FCSTD DOCUMENT  (FreeCAD 0.17R12435 (Git))
Label: X2SON-4_1x1mm_P0.65mm
License: All rights reserved
LicenseURL: http://en.wikipedia.org/wiki/All_rights_reserved
objects: Sketcher::SketchObject×6, App::Annotation×2, App::DocumentObjectGroup×1
note: 6 computed .brp shape members not serialized (recipe doc carries the construction recipe); baked Part::Feature solids carry a one-line shape summary decoded from their .brp

FEATURE [App::Annotation] Text  label="Ref#_0.6mm"
  LabelText = REF**
  Position = (0,1,0)
FEATURE [App::Annotation] Text001  label="Value#_1.00mm"
  LabelText = X2SON-4_1x1mm_P0.65mm
  Position = (0,-1.5,0)
FEATURE [Sketcher::SketchObject] Sketch001  label="F_Fab_0.1"
  MapMode = 2
  sketch-geometry (9):
    g0: LineSegment [constr] StartX=-0.5 StartY=0.5 StartZ=0 EndX=0.5 EndY=0.5 EndZ=0
    g1: LineSegment [constr] StartX=0.5 StartY=0.5 StartZ=0 EndX=0.5 EndY=-0.5 EndZ=0
    g2: LineSegment [constr] StartX=0.5 StartY=-0.5 StartZ=0 EndX=-0.5 EndY=-0.5 EndZ=0
    g3: LineSegment [constr] StartX=-0.5 StartY=-0.5 StartZ=0 EndX=-0.5 EndY=0.5 EndZ=0
    g4: LineSegment StartX=0.5 StartY=-0.5 StartZ=0 EndX=-0.5 EndY=-0.5 EndZ=0
    g5: LineSegment StartX=-0.5 StartY=-0.5 StartZ=0 EndX=-0.5 EndY=0.25 EndZ=0
    g6: LineSegment StartX=-0.5 StartY=0.25 StartZ=0 EndX=-0.25 EndY=0.5 EndZ=0
    g7: LineSegment StartX=-0.25 StartY=0.5 StartZ=0 EndX=0.5 EndY=0.5 EndZ=0
    g8: LineSegment StartX=0.5 StartY=0.5 StartZ=0 EndX=0.5 EndY=-0.5 EndZ=0
  constraints (22):
    c: Coincident(g0,g1)
    c: Coincident(g1,g2)
    c: Coincident(g2,g3)
    c: Coincident(g3,g0)
    c: Horizontal(g2)
    c: Vertical(g1)
    c: Equal(g0,g3)
    c: Symmetric(g0,g2,g-1)
    c: Symmetric(g0,g0,g-2)
    c: DistanceY(g3,g3) = 1
    c: Coincident(g1,g4)
    c: Coincident(g4,g2)
    c: Coincident(g4,g5)
    c: PointOnObject(g5,g3)
    c: Coincident(g5,g6)
    c: PointOnObject(g6,g0)
    c: Coincident(g6,g7)
    c: Coincident(g7,g0)
    c: Coincident(g7,g8)
    c: Coincident(g8,g4)
    c: DistanceX(g6,g6) = 0.25
    c: DistanceY(g6,g6) = 0.25
FEATURE [Sketcher::SketchObject] Sketch004  label="Pads_Poly_mask"
  MapMode = 5
  sketch-geometry (39):
    g0: LineSegment StartX=0.339411 StartY=0 StartZ=0 EndX=0 EndY=0.339411 EndZ=0
    g1: LineSegment StartX=0 StartY=0.339411 StartZ=0 EndX=-0.339411 EndY=0 EndZ=0
    g2: LineSegment StartX=-0.339411 StartY=0 StartZ=0 EndX=0 EndY=-0.339411 EndZ=0
    g3: LineSegment StartX=0 StartY=-0.339411 StartZ=0 EndX=0.339411 EndY=0 EndZ=0
    g4: Circle [constr] CenterX=0 CenterY=0 CenterZ=0 NormalX=0 NormalY=0 NormalZ=1 AngleXU=0 Radius=0.339411
    g5: Circle CenterX=0 CenterY=0 CenterZ=0 NormalX=0 NormalY=0 NormalZ=1 AngleXU=0 Radius=0.24
    g6: LineSegment StartX=-0.61 StartY=0.43 StartZ=0 EndX=-0.25 EndY=0.43 EndZ=0
    g7: LineSegment StartX=-0.25 StartY=0.43 StartZ=0 EndX=-0.25 EndY=0.4 EndZ=0
    g8: LineSegment StartX=-0.43 StartY=0.22 StartZ=0 EndX=-0.61 EndY=0.22 EndZ=0
    g9: LineSegment StartX=-0.61 StartY=0.22 StartZ=0 EndX=-0.61 EndY=0.43 EndZ=0
    g10: LineSegment StartX=-0.43 StartY=0.22 StartZ=0 EndX=-0.25 EndY=0.4 EndZ=0
    g11: LineSegment [constr] StartX=-0.43 StartY=0.325 StartZ=0 EndX=0.43 EndY=0.325 EndZ=0
    g12: LineSegment [constr] StartX=0.43 StartY=0.325 StartZ=0 EndX=0.43 EndY=-0.325 EndZ=0
    g13: LineSegment [constr] StartX=0.43 StartY=-0.325 StartZ=0 EndX=-0.43 EndY=-0.325 EndZ=0
    g14: LineSegment [constr] StartX=-0.43 StartY=-0.325 StartZ=0 EndX=-0.43 EndY=0.325 EndZ=0
    g15: LineSegment [constr] StartX=-0.5 StartY=0.5 StartZ=0 EndX=0.5 EndY=0.5 EndZ=0
    g16: LineSegment [constr] StartX=0.5 StartY=0.5 StartZ=0 EndX=0.5 EndY=-0.5 EndZ=0
    g17: LineSegment [constr] StartX=0.5 StartY=-0.5 StartZ=0 EndX=-0.5 EndY=-0.5 EndZ=0
    g18: LineSegment [constr] StartX=-0.5 StartY=-0.5 StartZ=0 EndX=-0.5 EndY=0.5 EndZ=0
    g19: LineSegment [constr] StartX=-0.25 StartY=0.4 StartZ=0 EndX=-0.0947056 EndY=0.244706 EndZ=0
    g20: LineSegment StartX=0.61 StartY=0.43 StartZ=0 EndX=0.25 EndY=0.43 EndZ=0
    g21: LineSegment StartX=0.25 StartY=0.43 StartZ=0 EndX=0.25 EndY=0.4 EndZ=0
    g22: LineSegment StartX=0.43 StartY=0.22 StartZ=0 EndX=0.61 EndY=0.22 EndZ=0
    g23: LineSegment StartX=0.61 StartY=0.22 StartZ=0 EndX=0.61 EndY=0.43 EndZ=0
    g24: LineSegment StartX=0.43 StartY=0.22 StartZ=0 EndX=0.25 EndY=0.4 EndZ=0
    g25: LineSegment StartX=0.61 StartY=-0.43 StartZ=0 EndX=0.25 EndY=-0.43 EndZ=0
    g26: LineSegment StartX=0.25 StartY=-0.43 StartZ=0 EndX=0.25 EndY=-0.4 EndZ=0
    g27: LineSegment StartX=0.43 StartY=-0.22 StartZ=0 EndX=0.61 EndY=-0.22 EndZ=0
    g28: LineSegment StartX=0.61 StartY=-0.22 StartZ=0 EndX=0.61 EndY=-0.43 EndZ=0
    g29: LineSegment StartX=0.43 StartY=-0.22 StartZ=0 EndX=0.25 EndY=-0.4 EndZ=0
    g30: LineSegment StartX=-0.61 StartY=-0.43 StartZ=0 EndX=-0.25 EndY=-0.43 EndZ=0
    g31: LineSegment StartX=-0.25 StartY=-0.43 StartZ=0 EndX=-0.25 EndY=-0.4 EndZ=0
    g32: LineSegment StartX=-0.43 StartY=-0.22 StartZ=0 EndX=-0.61 EndY=-0.22 EndZ=0
    g33: LineSegment StartX=-0.61 StartY=-0.22 StartZ=0 EndX=-0.61 EndY=-0.43 EndZ=0
    g34: LineSegment StartX=-0.43 StartY=-0.22 StartZ=0 EndX=-0.25 EndY=-0.4 EndZ=0
    g35: Circle CenterX=0.43 CenterY=-0.325 CenterZ=0 NormalX=0 NormalY=0 NormalZ=1 AngleXU=0 Radius=0.0742462
    g36: Circle CenterX=-0.43 CenterY=-0.325 CenterZ=0 NormalX=0 NormalY=0 NormalZ=1 AngleXU=0 Radius=0.0742462
    g37: Circle CenterX=-0.43 CenterY=0.325 CenterZ=0 NormalX=0 NormalY=0 NormalZ=1 AngleXU=0 Radius=0.0742462
    g38: Circle CenterX=0.43 CenterY=0.325 CenterZ=0 NormalX=0 NormalY=0 NormalZ=1 AngleXU=0 Radius=0.0742462
  constraints (114):
    c: Coincident(g0,g1)
    c: Coincident(g1,g2)
    c: Coincident(g2,g3)
    c: Coincident(g3,g0)
    c: Equal(g0,g1)
    c: Equal(g0,g2)
    c: Equal(g0,g3)
    c: PointOnObject(g0,g4)
    c: PointOnObject(g1,g4)
    c: PointOnObject(g2,g4)
    c: PointOnObject(g3,g4)
    c: Distance(g2) = 0.48
    c: Coincident(g4,g-1)
    c: PointOnObject(g0,g-1)
    c: Coincident(g5,g-1)
    c: Coincident(g6,g7)
    c: Coincident(g8,g9)
    c: Coincident(g9,g6)
    c: Horizontal(g6)
    c: Horizontal(g8)
    c: Vertical(g7)
    c: Vertical(g9)
    c: Coincident(g10,g7)
    c: Coincident(g10,g8)
    c: Parallel(g10,g1)
    c: DistanceX(g6,g6) = 0.36
    c: DistanceY(g9,g9) = 0.21
    c: DistanceX(g8,g8) = 0.18
    c: DistanceY(g7,g7) = 0.03
    c: Coincident(g11,g12)
    c: Coincident(g12,g13)
    c: Coincident(g13,g14)
    c: Coincident(g14,g11)
    c: Vertical(g12)
    c: Vertical(g14)
    c: Symmetric(g11,g11,g-2)
    c: Symmetric(g11,g12,g-1)
    c: DistanceX(g11,g11) = 0.86
    c: Coincident(g15,g16)
    c: Coincident(g16,g17)
    c: Coincident(g17,g18)
    c: Coincident(g18,g15)
    c: Horizontal(g15)
    c: Horizontal(g17)
    c: Vertical(g16)
    c: Vertical(g18)
    c: Symmetric(g15,g15,g-2)
    c: Symmetric(g15,g17,g-1)
    c: Equal(g18,g15)
    c: DistanceY(g18,g18) = 1
    c: PointOnObject(g8,g14)
    c: Symmetric(g6,g8,g11)
    c: Coincident(g19,g7)
    c: PointOnObject(g19,g1)
    c: Perpendicular(g10,g19)
    c: Distance(g19) = 0.219619
    c: Coincident(g20,g21)
    c: Coincident(g22,g23)
    c: Coincident(g23,g20)
    c: Horizontal(g20)
    c: Horizontal(g22)
    c: Vertical(g21)
    c: Vertical(g23)
    c: Coincident(g24,g21)
    c: Coincident(g24,g22)
    c: PointOnObject(g22,g12)
    c: Symmetric(g20,g22,g11)
    c: Equal(g20,g6)
    c: Equal(g23,g9)
    c: Equal(g22,g8)
    c: Parallel(g24,g0)
    c: Coincident(g30,g31)
    c: Coincident(g32,g33)
    c: Coincident(g33,g30)
    c: Horizontal(g30)
    c: Horizontal(g32)
    c: Vertical(g31)
    c: Vertical(g33)
    c: Coincident(g34,g31)
    c: Coincident(g34,g32)
    c: Coincident(g25,g26)
    c: Coincident(g27,g28)
    c: Coincident(g28,g25)
    c: Horizontal(g25)
    c: Horizontal(g27)
    c: Vertical(g26)
    c: Vertical(g28)
    c: Coincident(g29,g26)
    c: Coincident(g29,g27)
    c: Equal(g25,g30)
    c: Equal(g28,g33)
    c: Equal(g27,g32)
    c: PointOnObject(g27,g12)
    c: Equal(g8,g27)
    c: Equal(g27,g32)
    c: Equal(g28,g33)
    c: Equal(g33,g9)
    c: Equal(g6,g30)
    c: Equal(g30,g25)
    c: PointOnObject(g32,g14)
    c: Symmetric(g32,g30,g13)
    c: Symmetric(g27,g25,g13)
    c: Parallel(g3,g29)
    c: Parallel(g2,g34)
    c: Coincident(g35,g12)
    c: Coincident(g36,g13)
    c: Coincident(g37,g11)
    c: Coincident(g38,g11)
    c: Equal(g38,g35)
    c: Equal(g35,g36)
    c: Equal(g36,g37)
    c: DistanceY(g12,g12) = 0.65
    c: Tangent(g37,g10)
    c: Tangent(g5,g3)
FEATURE [Sketcher::SketchObject] Sketch005  label="Pads_Poly"
  ExternalGeometry = -> [Sketch004]
  MapMode = 5
  sketch-geometry (38):
    g0: LineSegment StartX=0 StartY=0.410122 StartZ=0 EndX=-0.410122 EndY=0 EndZ=0
    g1: LineSegment StartX=-0.410122 StartY=0 StartZ=0 EndX=0 EndY=-0.410122 EndZ=0
    g2: LineSegment StartX=0 StartY=-0.410122 StartZ=0 EndX=0.410122 EndY=0 EndZ=0
    g3: LineSegment StartX=0.410122 StartY=0 StartZ=0 EndX=0 EndY=0.410122 EndZ=0
    g4: LineSegment [constr] StartX=-0.339411 StartY=0 StartZ=0 EndX=-0.374767 EndY=-0.0353553 EndZ=0
    g5: LineSegment StartX=-0.2 StartY=0.379289 StartZ=0 EndX=-0.2 EndY=0.48 EndZ=0
    g6: LineSegment StartX=-0.2 StartY=0.48 StartZ=0 EndX=-0.66 EndY=0.48 EndZ=0
    g7: LineSegment StartX=-0.66 StartY=0.48 StartZ=0 EndX=-0.66 EndY=0.17 EndZ=0
    g8: LineSegment StartX=-0.66 StartY=0.17 StartZ=0 EndX=-0.409289 EndY=0.17 EndZ=0
    g9: LineSegment StartX=-0.409289 StartY=0.17 StartZ=0 EndX=-0.2 EndY=0.379289 EndZ=0
    g10: LineSegment [constr] StartX=-0.25 StartY=0.4 StartZ=0 EndX=-0.214645 EndY=0.364645 EndZ=0
    g11: LineSegment StartX=0.2 StartY=0.379289 StartZ=0 EndX=0.2 EndY=0.48 EndZ=0
    g12: LineSegment StartX=0.409289 StartY=0.17 StartZ=0 EndX=0.2 EndY=0.379289 EndZ=0
    g13: LineSegment StartX=0.66 StartY=0.17 StartZ=0 EndX=0.409289 EndY=0.17 EndZ=0
    g14: LineSegment StartX=0.66 StartY=0.48 StartZ=0 EndX=0.66 EndY=0.17 EndZ=0
    g15: LineSegment StartX=0.2 StartY=0.48 StartZ=0 EndX=0.66 EndY=0.48 EndZ=0
    g16: LineSegment StartX=0.2 StartY=-0.48 StartZ=0 EndX=0.66 EndY=-0.48 EndZ=0
    g17: LineSegment StartX=0.2 StartY=-0.379289 StartZ=0 EndX=0.2 EndY=-0.48 EndZ=0
    g18: LineSegment StartX=0.409289 StartY=-0.17 StartZ=0 EndX=0.2 EndY=-0.379289 EndZ=0
    g19: LineSegment StartX=0.66 StartY=-0.17 StartZ=0 EndX=0.409289 EndY=-0.17 EndZ=0
    g20: LineSegment StartX=0.66 StartY=-0.48 StartZ=0 EndX=0.66 EndY=-0.17 EndZ=0
    g21: LineSegment StartX=-0.409289 StartY=-0.17 StartZ=0 EndX=-0.2 EndY=-0.379289 EndZ=0
    g22: LineSegment StartX=-0.2 StartY=-0.379289 StartZ=0 EndX=-0.2 EndY=-0.48 EndZ=0
    g23: LineSegment StartX=-0.2 StartY=-0.48 StartZ=0 EndX=-0.66 EndY=-0.48 EndZ=0
    g24: LineSegment StartX=-0.66 StartY=-0.48 StartZ=0 EndX=-0.66 EndY=-0.17 EndZ=0
    g25: LineSegment StartX=-0.66 StartY=-0.17 StartZ=0 EndX=-0.409289 EndY=-0.17 EndZ=0
    g26: LineSegment [constr] StartX=0.25 StartY=0.4 StartZ=0 EndX=0.214645 EndY=0.364645 EndZ=0
    g27: LineSegment [constr] StartX=0.25 StartY=-0.4 StartZ=0 EndX=0.214645 EndY=-0.364645 EndZ=0
    g28: LineSegment [constr] StartX=-0.25 StartY=-0.4 StartZ=0 EndX=-0.214645 EndY=-0.364645 EndZ=0
    g29: LineSegment [constr] StartX=-0.61 StartY=0.43 StartZ=0 EndX=-0.61 EndY=0.48 EndZ=0
    g30: LineSegment [constr] StartX=0.61 StartY=0.43 StartZ=0 EndX=0.61 EndY=0.48 EndZ=0
    g31: LineSegment [constr] StartX=0.61 StartY=-0.43 StartZ=0 EndX=0.61 EndY=-0.48 EndZ=0
    g32: LineSegment [constr] StartX=-0.61 StartY=-0.43 StartZ=0 EndX=-0.61 EndY=-0.48 EndZ=0
    g33: Circle CenterX=-0.43 CenterY=0.325 CenterZ=0 NormalX=0 NormalY=0 NormalZ=1 AngleXU=0 Radius=0.124246
    g34: Circle CenterX=0.43 CenterY=0.325 CenterZ=0 NormalX=0 NormalY=0 NormalZ=1 AngleXU=0 Radius=0.124246
    g35: Circle CenterX=0.43 CenterY=-0.325 CenterZ=0 NormalX=0 NormalY=0 NormalZ=1 AngleXU=0 Radius=0.124246
    g36: Circle CenterX=-0.43 CenterY=-0.325 CenterZ=0 NormalX=0 NormalY=0 NormalZ=1 AngleXU=0 Radius=0.124246
    g37: Circle CenterX=0 CenterY=0 CenterZ=0 NormalX=0 NormalY=0 NormalZ=1 AngleXU=0 Radius=0.29
  constraints (109):
    c: PointOnObject(g0,g-2)
    c: PointOnObject(g0,g-1)
    c: Coincident(g0,g1)
    c: PointOnObject(g1,g-2)
    c: Coincident(g1,g2)
    c: Coincident(g2,g3)
    c: Coincident(g3,g0)
    c: PointOnObject(g2,g-1)
    c: Parallel(g2,g-19)
    c: Parallel(g-19,g0)
    c: Parallel(g-21,g1)
    c: PointOnObject(g4,g1)
    c: Perpendicular(g-21,g4)
    c: Distance(g4) = 0.05
    c: Coincident(g4,g-21)
    c: Vertical(g5)
    c: Coincident(g5,g6)
    c: Horizontal(g6)
    c: Coincident(g6,g7)
    c: Vertical(g7)
    c: Coincident(g7,g8)
    c: Horizontal(g8)
    c: Coincident(g8,g9)
    c: Coincident(g9,g5)
    c: Parallel(g9,g-7)
    c: DistanceY(g-9,g6) = 0.05
    c: DistanceX(g6,g-9) = 0.05
    c: DistanceY(g7,g-9) = 0.05
    c: DistanceX(g-8,g5) = 0.05
    c: Coincident(g10,g-7)
    c: PointOnObject(g10,g9)
    c: Perpendicular(g-7,g10)
    c: Distance(g10) = 0.05
    c: Vertical(g11)
    c: Coincident(g11,g15)
    c: Horizontal(g15)
    c: Coincident(g15,g14)
    c: Vertical(g14)
    c: Coincident(g14,g13)
    c: Horizontal(g13)
    c: Coincident(g13,g12)
    c: Coincident(g12,g11)
    c: Vertical(g22)
    c: Coincident(g22,g23)
    c: Horizontal(g23)
    c: Coincident(g23,g24)
    c: Vertical(g24)
    c: Coincident(g24,g25)
    c: Horizontal(g25)
    c: Coincident(g25,g21)
    c: Coincident(g21,g22)
    c: Vertical(g17)
    c: Coincident(g17,g16)
    c: Horizontal(g16)
    c: Coincident(g16,g20)
    c: Vertical(g20)
    c: Coincident(g20,g19)
    c: Horizontal(g19)
    c: Coincident(g19,g18)
    c: Coincident(g18,g17)
    c: Equal(g24,g7)
    c: Equal(g7,g14)
    c: Equal(g14,g20)
    c: Equal(g16,g23)
    c: Equal(g23,g6)
    c: Equal(g6,g15)
    c: Equal(g8,g25)
    c: Equal(g25,g19)
    c: Equal(g19,g13)
    c: Equal(g11,g5)
    c: Equal(g5,g22)
    c: Equal(g22,g17)
    c: Coincident(g26,g-12)
    c: PointOnObject(g26,g12)
    c: Coincident(g27,g-18)
    c: PointOnObject(g27,g18)
    c: Coincident(g28,g-17)
    c: PointOnObject(g28,g21)
    c: Perpendicular(g-17,g28)
    c: Perpendicular(g-18,g27)
    c: Perpendicular(g-12,g26)
    c: Equal(g26,g27)
    c: Equal(g27,g28)
    c: Equal(g28,g10)
    c: Coincident(g29,g-9)
    c: PointOnObject(g29,g6)
    c: Vertical(g29)
    c: Coincident(g30,g-11)
    c: PointOnObject(g30,g15)
    c: Vertical(g30)
    c: Coincident(g31,g-14)
    c: PointOnObject(g31,g16)
    c: Vertical(g31)
    c: Coincident(g32,g-16)
    c: PointOnObject(g32,g23)
    c: Vertical(g32)
    c: Equal(g32,g31)
    c: Equal(g31,g30)
    c: Equal(g30,g29)
    c: Coincident(g33,g-3)
    c: Coincident(g34,g-4)
    c: Coincident(g35,g-5)
    c: Tangent(g33,g9)
    c: Coincident(g36,g-6)
    c: Equal(g36,g35)
    c: Equal(g35,g34)
    c: Equal(g34,g33)
    c: Coincident(g37,g-1)
    c: Tangent(g37,g2)
FEATURE [Sketcher::SketchObject] Sketch002  label="F_CrtYd_0.05"
  ExternalGeometry = -> [Sketch001,Sketch005]
  sketch-geometry (4):
    g0: LineSegment StartX=-0.91 StartY=0.75 StartZ=0 EndX=0.91 EndY=0.75 EndZ=0
    g1: LineSegment StartX=0.91 StartY=0.75 StartZ=0 EndX=0.91 EndY=-0.75 EndZ=0
    g2: LineSegment StartX=0.91 StartY=-0.75 StartZ=0 EndX=-0.91 EndY=-0.75 EndZ=0
    g3: LineSegment StartX=-0.91 StartY=-0.75 StartZ=0 EndX=-0.91 EndY=0.75 EndZ=0
  constraints (12):
    c: Coincident(g0,g1)
    c: Coincident(g1,g2)
    c: Coincident(g2,g3)
    c: Coincident(g3,g0)
    c: Horizontal(g0)
    c: Horizontal(g2)
    c: Vertical(g1)
    c: Vertical(g3)
    c: DistanceX(g0,g-5) = 0.25
    c: DistanceX(g-6,g1) = 0.25
    c: DistanceY(g-3,g0) = 0.25
    c: DistanceY(g2,g-4) = 0.25
FEATURE [Sketcher::SketchObject] Sketch003  label="F_Silks_0.12"
  ExternalGeometry = -> [Sketch001,Sketch005]
  sketch-geometry (2):
    g0: LineSegment StartX=-0.66 StartY=0.63 StartZ=0 EndX=0.5 EndY=0.63 EndZ=0
    g1: LineSegment StartX=-0.5 StartY=-0.63 StartZ=0 EndX=0.5 EndY=-0.63 EndZ=0
  constraints (8):
    c: Horizontal(g0)
    c: Horizontal(g1)
    c: PointOnObject(g0,g-6)
    c: PointOnObject(g0,g-4)
    c: PointOnObject(g1,g-4)
    c: PointOnObject(g1,g-5)
    c: DistanceY(g1,g-7) = 0.15
    c: DistanceY(g-6,g0) = 0.15
FEATURE [Sketcher::SketchObject] Sketch006  label="Pads_Poly_paste"
  ExternalGeometry = -> [Sketch004]
  MapMode = 5
  sketch-geometry (20):
    g0: LineSegment StartX=-0.65 StartY=0.22 StartZ=0 EndX=-0.43 EndY=0.22 EndZ=0
    g1: LineSegment StartX=-0.43 StartY=0.22 StartZ=0 EndX=-0.25 EndY=0.4 EndZ=0
    g2: LineSegment StartX=-0.25 StartY=0.4 StartZ=0 EndX=-0.25 EndY=0.43 EndZ=0
    g3: LineSegment StartX=-0.25 StartY=0.43 StartZ=0 EndX=-0.65 EndY=0.43 EndZ=0
    g4: LineSegment StartX=-0.65 StartY=0.43 StartZ=0 EndX=-0.65 EndY=0.22 EndZ=0
    g5: LineSegment StartX=0.25 StartY=0.43 StartZ=0 EndX=0.65 EndY=0.43 EndZ=0
    g6: LineSegment StartX=0.25 StartY=0.4 StartZ=0 EndX=0.25 EndY=0.43 EndZ=0
    g7: LineSegment StartX=0.43 StartY=0.22 StartZ=0 EndX=0.25 EndY=0.4 EndZ=0
    g8: LineSegment StartX=0.65 StartY=0.22 StartZ=0 EndX=0.43 EndY=0.22 EndZ=0
    g9: LineSegment StartX=0.65 StartY=0.43 StartZ=0 EndX=0.65 EndY=0.22 EndZ=0
    g10: LineSegment StartX=0.65 StartY=-0.22 StartZ=0 EndX=0.43 EndY=-0.22 EndZ=0
    g11: LineSegment StartX=0.65 StartY=-0.43 StartZ=0 EndX=0.65 EndY=-0.22 EndZ=0
    g12: LineSegment StartX=0.25 StartY=-0.43 StartZ=0 EndX=0.65 EndY=-0.43 EndZ=0
    g13: LineSegment StartX=0.25 StartY=-0.4 StartZ=0 EndX=0.25 EndY=-0.43 EndZ=0
    g14: LineSegment StartX=0.43 StartY=-0.22 StartZ=0 EndX=0.25 EndY=-0.4 EndZ=0
    g15: LineSegment StartX=-0.43 StartY=-0.22 StartZ=0 EndX=-0.25 EndY=-0.4 EndZ=0
    g16: LineSegment StartX=-0.25 StartY=-0.4 StartZ=0 EndX=-0.25 EndY=-0.43 EndZ=0
    g17: LineSegment StartX=-0.25 StartY=-0.43 StartZ=0 EndX=-0.65 EndY=-0.43 EndZ=0
    g18: LineSegment StartX=-0.65 StartY=-0.43 StartZ=0 EndX=-0.65 EndY=-0.22 EndZ=0
    g19: LineSegment StartX=-0.65 StartY=-0.22 StartZ=0 EndX=-0.43 EndY=-0.22 EndZ=0
  constraints (48):
    c: Coincident(g0,g-9)
    c: Horizontal(g0)
    c: Coincident(g0,g1)
    c: Coincident(g1,g-9)
    c: Coincident(g1,g2)
    c: Coincident(g2,g-10)
    c: Coincident(g2,g3)
    c: Horizontal(g3)
    c: Coincident(g3,g4)
    c: Coincident(g4,g0)
    c: Vertical(g4)
    c: DistanceX(g3,g3) = 0.4
    c: Horizontal(g8)
    c: Coincident(g8,g7)
    c: Coincident(g7,g6)
    c: Coincident(g6,g5)
    c: Horizontal(g5)
    c: Coincident(g5,g9)
    c: Coincident(g9,g8)
    c: Vertical(g9)
    c: Horizontal(g19)
    c: Coincident(g19,g15)
    c: Coincident(g15,g16)
    c: Coincident(g16,g17)
    c: Horizontal(g17)
    c: Coincident(g17,g18)
    c: Coincident(g18,g19)
    c: Vertical(g18)
    c: Horizontal(g10)
    c: Coincident(g10,g14)
    c: Coincident(g14,g13)
    c: Coincident(g13,g12)
    c: Horizontal(g12)
    c: Coincident(g12,g11)
    c: Coincident(g11,g10)
    c: Vertical(g11)
    c: Coincident(g15,g-3)
    c: Coincident(g15,g-3)
    c: Coincident(g16,g-4)
    c: Coincident(g13,g-6)
    c: Coincident(g12,g-5)
    c: Coincident(g10,g-6)
    c: Coincident(g6,g-7)
    c: Coincident(g5,g-8)
    c: Coincident(g7,g-7)
    c: Equal(g5,g12)
    c: Equal(g12,g17)
    c: Equal(g17,g3)
FEATURE [App::DocumentObjectGroup] Group  label="X2SON-4_1x1mm_P0.65mm"
  Group = -> [Text,Text001,Sketch001,Sketch002,Sketch003,Sketch004,Sketch005,Sketch006]
